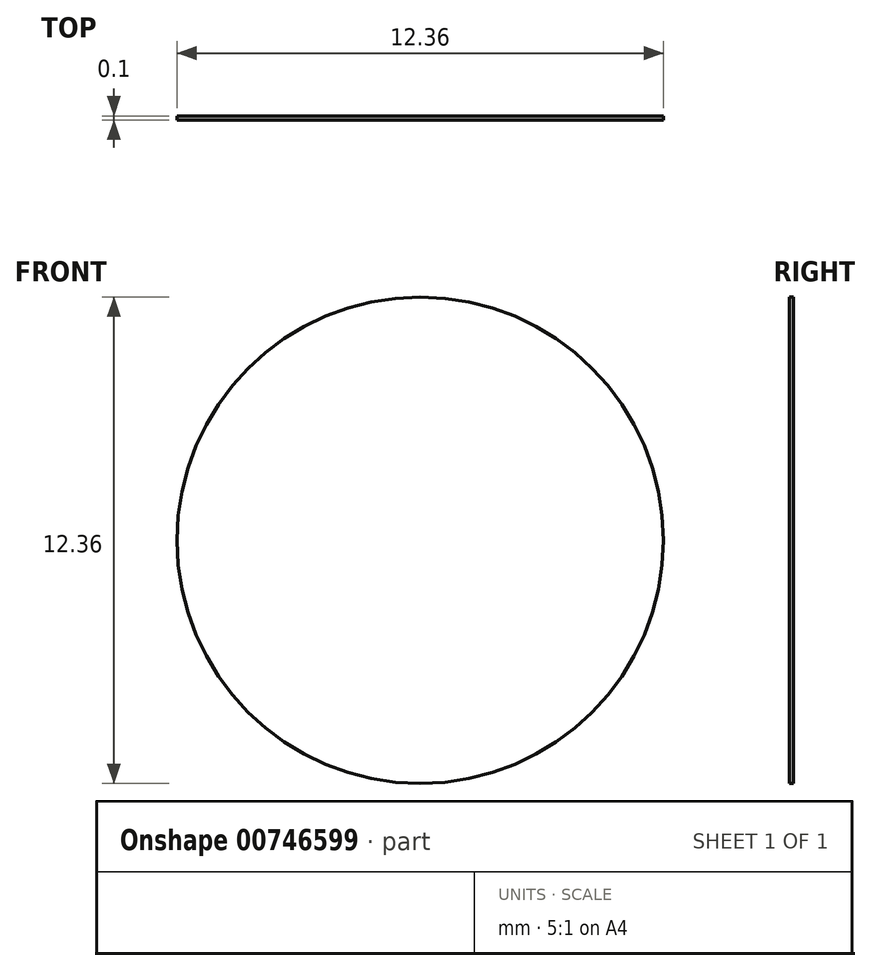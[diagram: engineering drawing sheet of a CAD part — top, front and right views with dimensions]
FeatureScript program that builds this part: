
annotation { "Feature Type Name" : "Feature", "Feature Type Description" : "" }
export const myFeature = defineFeature(function(context is Context, id is Id, definition is map)
    precondition{}
    {
        {
            var Q0;
            Q0=qCreatedBy(makeId("Front.planeOp"),FACE);
            var sketch = newSketch(context, id + "F0", { "sketchPlane" : qUnion([Q0])});
            skCircle(sketch, "E0", {"center": v(0, 0) * mm, "radius": 6.18 * mm});
            skSolve(sketch);
        }
        {
            var Q0;
            Q0 = qSketchRegion(id + "F0", true);
            extrude(context, id + "F1", {"entities" : qUnion([Q0]), "depth" : .10 * mm, "offsetDistance" : 25 * mm});
        }
    });
